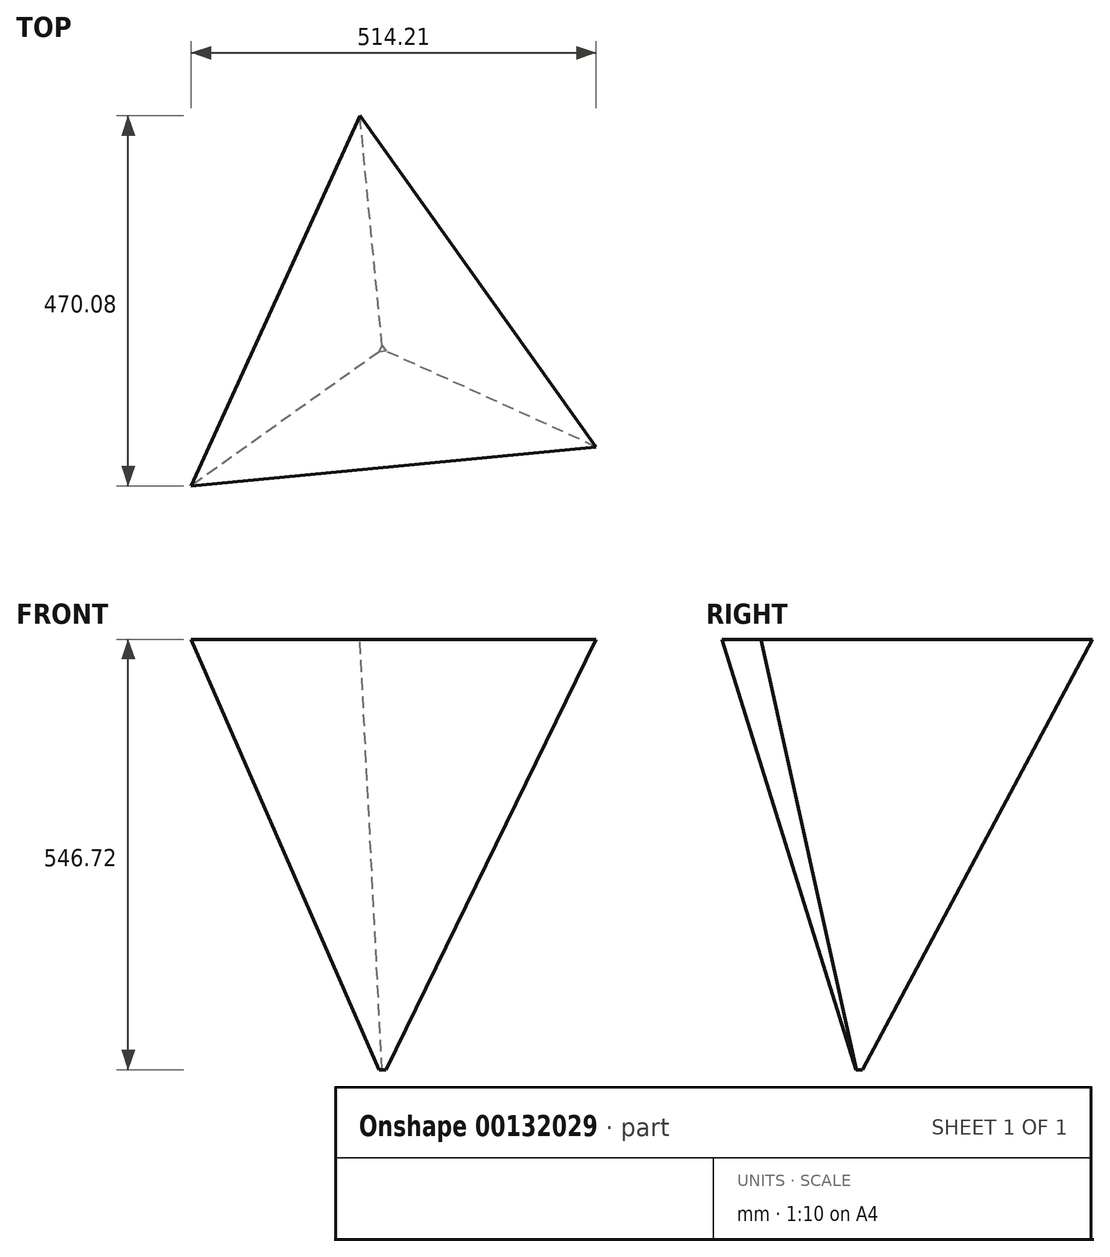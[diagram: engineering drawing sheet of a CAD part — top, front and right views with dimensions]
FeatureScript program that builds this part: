
annotation { "Feature Type Name" : "Feature", "Feature Type Description" : "" }
export const myFeature = defineFeature(function(context is Context, id is Id, definition is map)
    precondition{}
    {
        {
            var Q0;
            Q0=qCreatedBy(makeId("Top.planeOp"),FACE);
            var sketch = newSketch(context, id + "F0", { "sketchPlane" : qUnion([Q0])});
            skLineSegment(sketch, "E0", {"start": v(-17.37, 67.1) * mm, "end": v(-70.03, -48.48) * mm});
            skLineSegment(sketch, "E1", {"start": v(-17.37, 67.1) * mm, "end": v(56.38, -36.3) * mm});
            skLineSegment(sketch, "E2", {"start": v(56.38, -36.3) * mm, "end": v(-70.03, -48.48) * mm});
            skSolve(sketch);
        }
        {
            var Q0;
            Q0 = qSketchRegion(id + "F0", true);
            extrude(context, id + "F1", {"entities" : qUnion([Q0]), "depth" : 419.72 * mm, "hasDraft" : true, "draftAngle" : 15 * degree, "hasSecondDirection" : true, "secondDirectionOppositeDirection" : true, "secondDirectionDepth" : 127 * mm, "hasSecondDirectionDraft" : true, "secondDirectionDraftAngle" : 15 * degree, "secondDirectionDraftPullDirection" : true});
        }
    });
